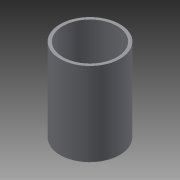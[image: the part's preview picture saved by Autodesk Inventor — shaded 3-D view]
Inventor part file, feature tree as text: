
AUTODESK INVENTOR PART (.ipt)
format: ipt  version: 2015 (Build 190159000, 159)  size: 96,768 bytes
history: native  units: mm
features: extrude x1, shell x1, fillet x1, sketch x1
ambient origin geometry x8: Origin, YZ Plane, XZ Plane, XY Plane, X Axis, Y Axis, Z Axis, Center Point
bodies: Solid1 (feature_tree)
feature tree (4):
  extrude  "Extrusion1"  Depth=140.0mm TaperAngle=0.0deg
  shell  "Shell1"  Thickness=5.0mm
  fillet  "Fillet1"  Radius=2.0mm
  sketch  "Sketch1"  dims[d0=100.0mm d1=140.0mm d2=0.0mm d3=5.0mm d4=2.0mm]
